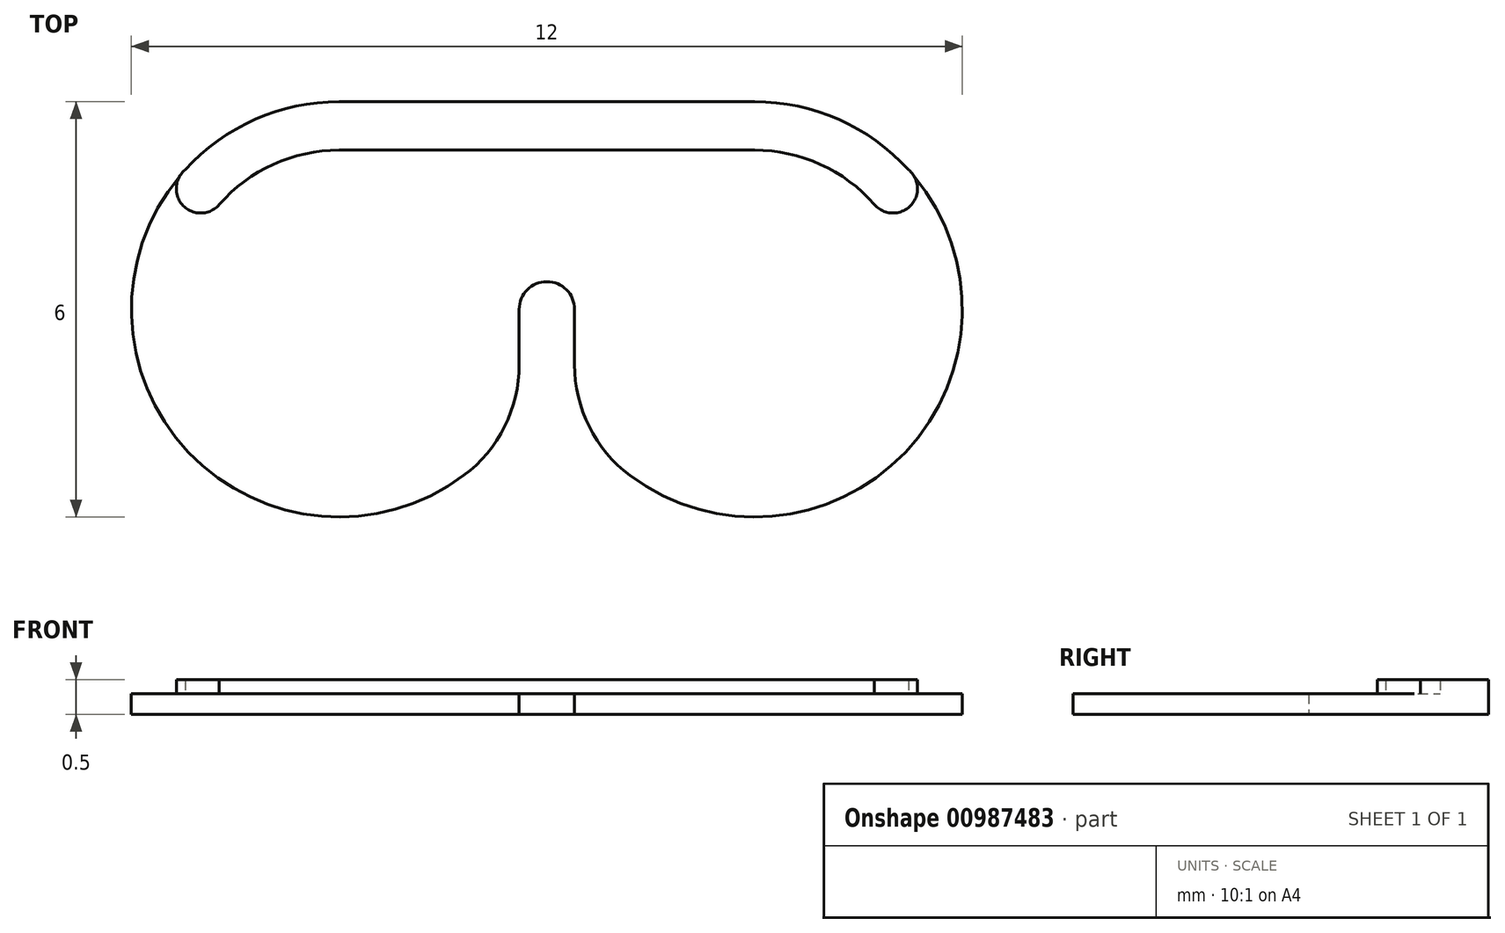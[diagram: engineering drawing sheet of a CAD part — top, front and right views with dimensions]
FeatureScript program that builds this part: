
annotation { "Feature Type Name" : "Feature", "Feature Type Description" : "" }
export const myFeature = defineFeature(function(context is Context, id is Id, definition is map)
    precondition{}
    {
        {
            var Q0;
            Q0=qCreatedBy(makeId("Top.planeOp"),FACE);
            var sketch = newSketch(context, id + "F0", { "sketchPlane" : qUnion([Q0])});
            skArc(sketch, "E0", {"start": v(-3, 3) * mm, "mid": v(-5.6, -1.5) * mm, "end": v(-0.4, -1.5) * mm});
            skArc(sketch, "E1.MirrorC", {"start": v(3, 3) * mm, "mid": v(5.6, -1.5) * mm, "end": v(0.4, -1.5) * mm});
            skLineSegment(sketch, "E2", {"start": v(-3, 3) * mm, "end": v(3, 3) * mm});
            skArc(sketch, "E3", {"start": v(0.4, 0) * mm, "mid": v(0, 0.4) * mm, "end": v(-0.4, 0) * mm});
            skLineSegment(sketch, "E4", {"start": v(-0.4, 0) * mm, "end": v(-0.4, -1.5) * mm});
            skLineSegment(sketch, "E5", {"start": v(0.4, 0) * mm, "end": v(0.4, -1.5) * mm});
            skSolve(sketch);
        }
        {
            var Q0;
            Q0 = qSketchRegion(id + "F0", true);
            extrude(context, id + "F1", {"entities" : qUnion([Q0]), "depth" : 0.3 * mm, "offsetDistance" : 25 * mm});
        }
        {
            var Q0;
            Q0=makeQuery(id+"F1.opExtrude","CAP_FACE",FACE,{"disambiguationData":[OSD([sQuery(id+"F0.wireOp",EDGE,"E0"),sQuery(id+"F0.wireOp",EDGE,"E1.MirrorC"),sQuery(id+"F0.wireOp",EDGE,"E2")])],"isStart":false});
            cPlane(context, id + "F2", {"entities" : qUnion([Q0]), "cplaneType" : CPlaneType.OFFSET, "offset" : 0.2 * mm, "width" : 150 * mm, "height" : 150 * mm});
        }
        {
            var Q0;
            Q0=makeQuery(id+"F1.opExtrude","SWEPT_EDGE",EDGE,{"disambiguationData":[OSD([sQuery(id+"F0.wireOp",EDGE,"E0"),sQuery(id+"F0.wireOp",EDGE,"E4")])]});
            var Q1;
            Q1=makeQuery(id+"F1.opExtrude","SWEPT_EDGE",EDGE,{"disambiguationData":[OSD([sQuery(id+"F0.wireOp",EDGE,"E1.MirrorC"),sQuery(id+"F0.wireOp",EDGE,"E5")])]});
            fillet(context, id + "F3", {"entities" : qUnion([Q0, Q1]), "tangentPropagation" : true, "radius" : 2 * mm, "defaultsChanged" : true, "vertexSettings" : [], "allowEdgeOverflow" : false});
        }
        {
            var Q0;
            Q0=makeQuery(id+"F1.opExtrude","CAP_FACE",FACE,{"disambiguationData":[OSD([sQuery(id+"F0.wireOp",EDGE,"E0"),sQuery(id+"F0.wireOp",EDGE,"E1.MirrorC"),sQuery(id+"F0.wireOp",EDGE,"E2"),sQuery(id+"F0.wireOp",EDGE,"E3"),sQuery(id+"F0.wireOp",EDGE,"E4"),sQuery(id+"F0.wireOp",EDGE,"E5")])],"isStart":false});
            var sketch = newSketch(context, id + "F4", { "sketchPlane" : qUnion([Q0])});
            skArc(sketch, "E6.0", {"start": v(3, 3) * mm, "mid": v(4.27, 2.72) * mm, "end": v(5.3, 1.92) * mm});
            skLineSegment(sketch, "E6.1", {"start": v(-3, 3) * mm, "end": v(3, 3) * mm});
            skArc(sketch, "E6.2", {"start": v(-3, 3) * mm, "mid": v(-4.27, 2.72) * mm, "end": v(-5.3, 1.92) * mm});
            skArc(sketch, "E7.0", {"start": v(3, 2.3) * mm, "mid": v(3.95, 2.1) * mm, "end": v(4.74, 1.5) * mm});
            skLineSegment(sketch, "E7.1", {"start": v(-3, 2.3) * mm, "end": v(3, 2.3) * mm});
            skArc(sketch, "E7.2", {"start": v(-3, 2.3) * mm, "mid": v(-3.95, 2.1) * mm, "end": v(-4.74, 1.5) * mm});
            skArc(sketch, "E8", {"start": v(-5.22, 2.02) * mm, "mid": v(-5.25, 1.5) * mm, "end": v(-4.73, 1.51) * mm});
            skLineSegment(sketch, "E9", {"start": v(0, 0) * mm, "end": v(0, 1.27) * mm, "construction": true});
            skArc(sketch, "E10.MirrorCS", {"start": v(5.22, 2.02) * mm, "mid": v(5.25, 1.5) * mm, "end": v(4.73, 1.51) * mm});
            skPoint(sketch, "E11.orphan", {"position": v(-1.2, -2.4) * mm});
            skPoint(sketch, "E12.orphan", {"position": v(1.2, -2.4) * mm});
            skSolve(sketch);
        }
        {
            var Q0;
            Q0 = qSketchRegion(id + "F4", true);
            extrude(context, id + "F5", {"entities" : qUnion([Q0]), "operationType" : NewBodyOperationType.ADD, "depth" : 0.2 * mm, "offsetDistance" : 25 * mm});
        }
    });
